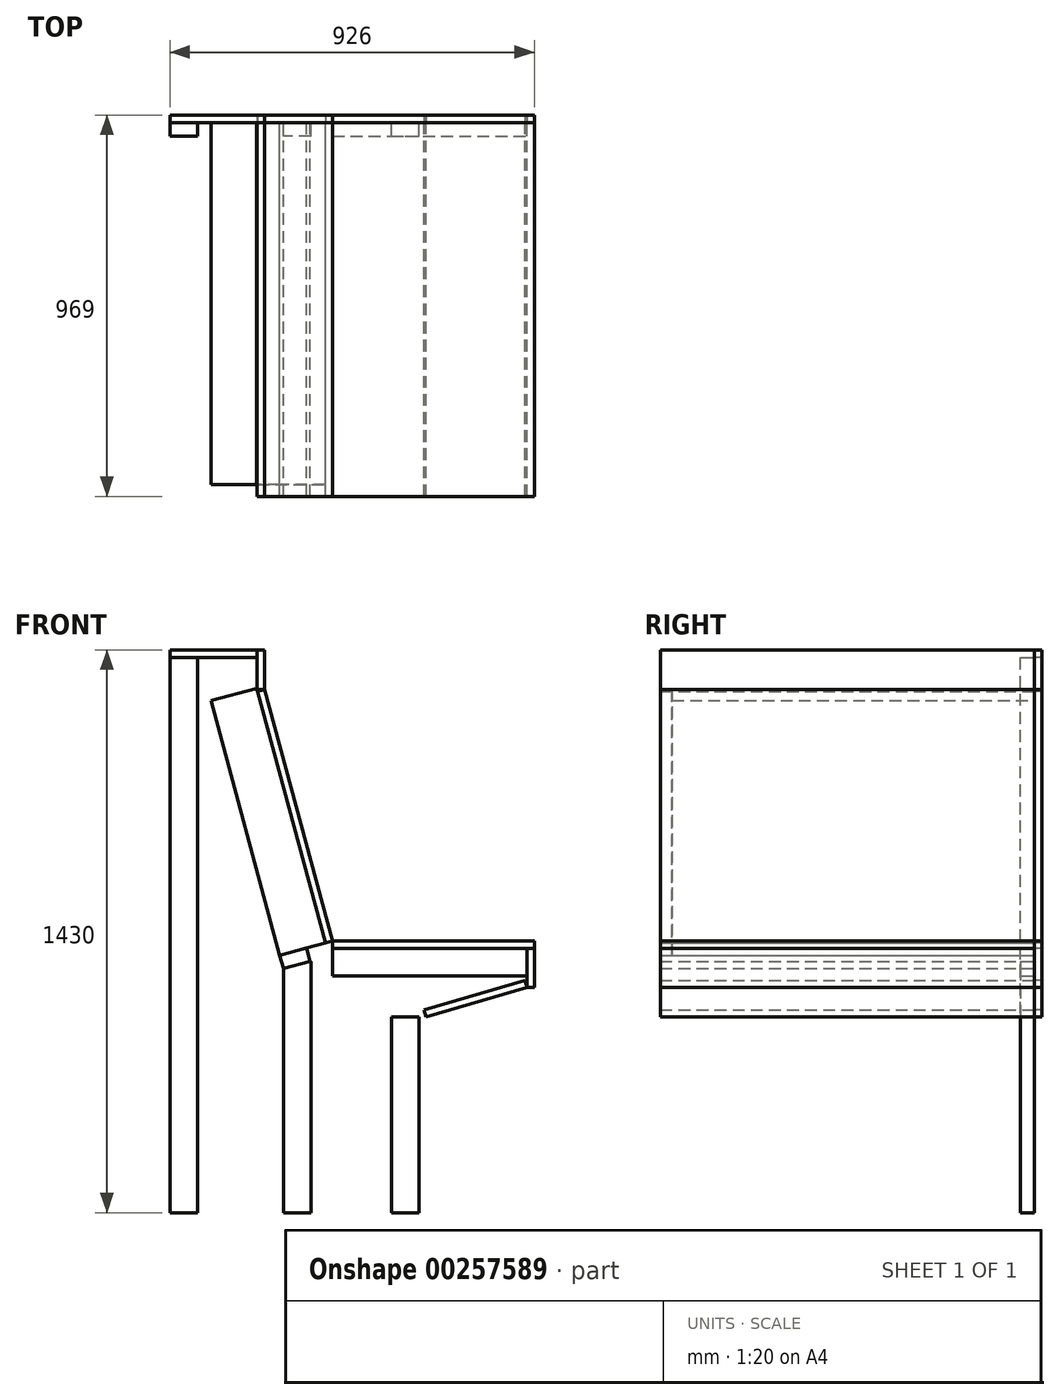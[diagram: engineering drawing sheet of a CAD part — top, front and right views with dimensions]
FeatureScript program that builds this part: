
annotation { "Feature Type Name" : "Feature", "Feature Type Description" : "" }
export const myFeature = defineFeature(function(context is Context, id is Id, definition is map)
    precondition{}
    {
        {
            var Q0;
            Q0=qCreatedBy(makeId("Front.planeOp"),FACE);
            var sketch = newSketch(context, id + "F0", { "sketchPlane" : qUnion([Q0])});
            skLineSegment(sketch, "E0", {"start": v(0, 0) * mm, "end": v(0, 1430) * mm});
            skLineSegment(sketch, "E1", {"start": v(0, 1430) * mm, "end": v(270, 1430) * mm});
            skLineSegment(sketch, "E2", {"start": v(270, 1430) * mm, "end": v(270, 1349.88) * mm});
            skLineSegment(sketch, "E3", {"start": v(275.18, 1310.8) * mm, "end": v(436, 714.79) * mm});
            skLineSegment(sketch, "E4", {"start": v(455.32, 700) * mm, "end": v(935, 700) * mm});
            skLineSegment(sketch, "E5", {"start": v(955, 680) * mm, "end": v(955, 585.01) * mm});
            skLineSegment(sketch, "E6", {"start": v(940.59, 565.8) * mm, "end": v(694.41, 494.2) * mm});
            skLineSegment(sketch, "E7", {"start": v(680, 474.99) * mm, "end": v(680, 0) * mm});
            skLineSegment(sketch, "E8", {"start": v(680, 0) * mm, "end": v(0, 0) * mm});
            skPoint(sketch, "E9.visualSharp", {"position": v(270, 1430) * mm});
            skPoint(sketch, "E10.visualSharp", {"position": v(270, 1330) * mm});
            skArc(sketch, "E10.filletArc", {"start": v(270, 1349.88) * mm, "mid": v(271.3, 1330.17) * mm, "end": v(275.18, 1310.8) * mm});
            skPoint(sketch, "E11.visualSharp", {"position": v(440, 700) * mm});
            skArc(sketch, "E11.filletArc", {"start": v(436, 714.79) * mm, "mid": v(443.16, 704.12) * mm, "end": v(455.32, 700) * mm});
            skPoint(sketch, "E12.visualSharp", {"position": v(955, 700) * mm});
            skArc(sketch, "E12.filletArc", {"start": v(955, 680) * mm, "mid": v(949.14, 694.14) * mm, "end": v(935, 700) * mm});
            skPoint(sketch, "E13.visualSharp", {"position": v(955, 570) * mm});
            skArc(sketch, "E13.filletArc", {"start": v(940.59, 565.8) * mm, "mid": v(951, 573) * mm, "end": v(955, 585.01) * mm});
            skPoint(sketch, "E14.visualSharp", {"position": v(680, 490) * mm});
            skArc(sketch, "E14.filletArc", {"start": v(694.41, 494.2) * mm, "mid": v(684, 487) * mm, "end": v(680, 474.99) * mm});
            skLineSegment(sketch, "E15.bottom", {"start": v(0, 0) * mm, "end": v(19, 0) * mm});
            skLineSegment(sketch, "E15.top", {"start": v(0, 1430) * mm, "end": v(19, 1430) * mm});
            skLineSegment(sketch, "E15.right", {"start": v(19, 0) * mm, "end": v(19, 1430) * mm});
            skLineSegment(sketch, "E16.bottom", {"start": v(670, 0) * mm, "end": v(652, 0) * mm});
            skLineSegment(sketch, "E16.top", {"start": v(670, 497.5) * mm, "end": v(652, 497.5) * mm});
            skLineSegment(sketch, "E16.left", {"start": v(670, 0) * mm, "end": v(670, 497.5) * mm});
            skLineSegment(sketch, "E16.right", {"start": v(652, 0) * mm, "end": v(652, 497.5) * mm});
            skLineSegment(sketch, "E17", {"start": v(670, 497.5) * mm, "end": v(926, 571.98) * mm});
            skLineSegment(sketch, "E18", {"start": v(926, 571.98) * mm, "end": v(920.7, 590.22) * mm});
            skLineSegment(sketch, "E19", {"start": v(920.7, 590.22) * mm, "end": v(664.7, 515.75) * mm});
            skLineSegment(sketch, "E20", {"start": v(664.7, 515.75) * mm, "end": v(670, 497.5) * mm});
            skLineSegment(sketch, "E21.bottom", {"start": v(926, 571.98) * mm, "end": v(945, 571.98) * mm});
            skLineSegment(sketch, "E21.top", {"start": v(926, 671) * mm, "end": v(945, 671) * mm});
            skLineSegment(sketch, "E21.left", {"start": v(926, 571.98) * mm, "end": v(926, 671) * mm});
            skLineSegment(sketch, "E21.right", {"start": v(945, 571.98) * mm, "end": v(945, 671) * mm});
            skLineSegment(sketch, "E22.bottom", {"start": v(945, 671) * mm, "end": v(432.34, 671) * mm});
            skLineSegment(sketch, "E22.top", {"start": v(945, 690) * mm, "end": v(432.34, 690) * mm});
            skLineSegment(sketch, "E22.left", {"start": v(945, 671) * mm, "end": v(945, 690) * mm});
            skLineSegment(sketch, "E22.right", {"start": v(432.34, 671) * mm, "end": v(432.34, 690) * mm});
            skLineSegment(sketch, "E23", {"start": v(432.34, 690) * mm, "end": v(260, 1328.67) * mm});
            skLineSegment(sketch, "E24", {"start": v(260, 1328.67) * mm, "end": v(241.66, 1323.72) * mm});
            skLineSegment(sketch, "E25", {"start": v(241.66, 1323.72) * mm, "end": v(414, 685.05) * mm});
            skLineSegment(sketch, "E26", {"start": v(414, 685.05) * mm, "end": v(432.34, 690) * mm});
            skLineSegment(sketch, "E27.bottom", {"start": v(260, 1328.67) * mm, "end": v(241, 1328.67) * mm});
            skLineSegment(sketch, "E27.top", {"start": v(260, 1430) * mm, "end": v(241, 1430) * mm});
            skLineSegment(sketch, "E27.left", {"start": v(260, 1328.67) * mm, "end": v(260, 1430) * mm});
            skLineSegment(sketch, "E27.right", {"start": v(241, 1328.67) * mm, "end": v(241, 1430) * mm});
            skLineSegment(sketch, "E28.bottom", {"start": v(241, 1430) * mm, "end": v(19, 1430) * mm});
            skLineSegment(sketch, "E28.top", {"start": v(241, 1411) * mm, "end": v(19, 1411) * mm});
            skLineSegment(sketch, "E28.left", {"start": v(241, 1430) * mm, "end": v(241, 1411) * mm});
            skLineSegment(sketch, "E28.right", {"start": v(19, 1430) * mm, "end": v(19, 1411) * mm});
            skSolve(sketch);
        }
        {
            var Q0;
            Q0=makeQuery(id+"F0.imprint","IMPRINT",FACE,{"disambiguationData":[TD([[makeQuery(id+"F0.imprint","IMPRINT",EDGE,{"derivedFrom":sQuery(id+"F0.wireOp",EDGE,"E23")}),1.0]])]});
            var Q1;
            Q1=makeQuery(id+"F0.imprint","IMPRINT",FACE,{"disambiguationData":[TD([[makeQuery(id+"F0.imprint","IMPRINT",EDGE,{"derivedFrom":sQuery(id+"F0.wireOp",EDGE,"E22.top")}),1.0]])]});
            var Q2;
            Q2=makeQuery(id+"F0.imprint","IMPRINT",FACE,{"disambiguationData":[TD([[makeQuery(id+"F0.imprint","IMPRINT",EDGE,{"derivedFrom":sQuery(id+"F0.wireOp",EDGE,"E17")}),1.0]])]});
            var Q3;
            Q3=makeQuery(id+"F0.imprint","IMPRINT",FACE,{"disambiguationData":[TD([[makeQuery(id+"F0.imprint","IMPRINT",EDGE,{"derivedFrom":sQuery(id+"F0.wireOp",EDGE,"E16.bottom")}),-1.0]])]});
            var Q4;
            Q4=makeQuery(id+"F0.imprint","IMPRINT",FACE,{"disambiguationData":[TD([[makeQuery(id+"F0.imprint","IMPRINT",EDGE,{"derivedFrom":sQuery(id+"F0.wireOp",EDGE,"E15.bottom")}),1.0]])]});
            var Q5;
            Q5=makeQuery(id+"F0.imprint","IMPRINT",FACE,{"disambiguationData":[TD([[makeQuery(id+"F0.imprint","IMPRINT",EDGE,{"derivedFrom":sQuery(id+"F0.wireOp",EDGE,"E28.bottom")}),1.0]])]});
            var Q6;
            Q6=makeQuery(id+"F0.imprint","IMPRINT",FACE,{"disambiguationData":[TD([[makeQuery(id+"F0.imprint","IMPRINT",EDGE,{"derivedFrom":sQuery(id+"F0.wireOp",EDGE,"E27.bottom")}),-1.0]])]});
            var Q7;
            Q7=makeQuery(id+"F0.imprint","IMPRINT",FACE,{"disambiguationData":[TD([[makeQuery(id+"F0.imprint","IMPRINT",EDGE,{"derivedFrom":sQuery(id+"F0.wireOp",EDGE,"E1")}),-1.0]])]});
            var Q8;
            Q8=makeQuery(id+"F0.imprint","IMPRINT",FACE,{"disambiguationData":[TD([[makeQuery(id+"F0.imprint","IMPRINT",EDGE,{"derivedFrom":sQuery(id+"F0.wireOp",EDGE,"E21.bottom")}),1.0]])]});
            var Q9;
            {var subQ3=sQuery(id+"F0.wireOp",EDGE,"E15.right");Q9=makeQuery(id+"F0.imprint","IMPRINT",FACE,{"disambiguationData":[TD([[makeQuery(id+"F0.imprint","IMPRINT",EDGE,{"derivedFrom":subQ3}),-1.0]])]});}
            extrude(context, id + "F1", {"entities" : qUnion([Q0, Q1, Q2, Q3, Q4, Q5, Q6, Q7, Q8, Q9]), "oppositeDirection" : true, "depth" : 19 * mm});
        }
        {
            var Q0;
            Q0=makeQuery(id+"F0.imprint","IMPRINT",FACE,{"disambiguationData":[TD([[makeQuery(id+"F0.imprint","IMPRINT",EDGE,{"derivedFrom":sQuery(id+"F0.wireOp",EDGE,"E15.bottom")}),1.0]])]});
            var Q1;
            Q1=makeQuery(id+"F0.imprint","IMPRINT",FACE,{"disambiguationData":[TD([[makeQuery(id+"F0.imprint","IMPRINT",EDGE,{"derivedFrom":sQuery(id+"F0.wireOp",EDGE,"E16.bottom")}),-1.0]])]});
            var Q2;
            Q2=makeQuery(id+"F0.imprint","IMPRINT",FACE,{"disambiguationData":[TD([[makeQuery(id+"F0.imprint","IMPRINT",EDGE,{"derivedFrom":sQuery(id+"F0.wireOp",EDGE,"E17")}),1.0]])]});
            var Q3;
            Q3=makeQuery(id+"F0.imprint","IMPRINT",FACE,{"disambiguationData":[TD([[makeQuery(id+"F0.imprint","IMPRINT",EDGE,{"derivedFrom":sQuery(id+"F0.wireOp",EDGE,"E22.top")}),1.0]])]});
            var Q4;
            Q4=makeQuery(id+"F0.imprint","IMPRINT",FACE,{"disambiguationData":[TD([[makeQuery(id+"F0.imprint","IMPRINT",EDGE,{"derivedFrom":sQuery(id+"F0.wireOp",EDGE,"E23")}),1.0]])]});
            var Q5;
            Q5=makeQuery(id+"F0.imprint","IMPRINT",FACE,{"disambiguationData":[TD([[makeQuery(id+"F0.imprint","IMPRINT",EDGE,{"derivedFrom":sQuery(id+"F0.wireOp",EDGE,"E27.bottom")}),-1.0]])]});
            extrude(context, id + "F2", {"entities" : qUnion([Q0, Q1, Q2, Q3, Q4, Q5]), "depth" : 950 * mm});
        }
        {
            var Q0;
            Q0=makeQuery(id+"F0.imprint","IMPRINT",FACE,{"disambiguationData":[TD([[makeQuery(id+"F0.imprint","IMPRINT",EDGE,{"derivedFrom":sQuery(id+"F0.wireOp",EDGE,"E21.bottom")}),1.0]])]});
            var Q1;
            Q1=makeQuery(id+"F0.imprint","IMPRINT",FACE,{"disambiguationData":[TD([[makeQuery(id+"F0.imprint","IMPRINT",EDGE,{"derivedFrom":sQuery(id+"F0.wireOp",EDGE,"E28.bottom")}),1.0]])]});
            extrude(context, id + "F3", {"entities" : qUnion([Q0, Q1]), "depth" : 950 * mm});
        }
        {
            var Q0;
            Q0=qCreatedBy(makeId("Front.planeOp"),FACE);
            var sketch = newSketch(context, id + "F4", { "sketchPlane" : qUnion([Q0])});
            skLineSegment(sketch, "E29", {"start": v(239.45, 1331.91) * mm, "end": v(414, 685.05) * mm});
            skLineSegment(sketch, "E30", {"start": v(414, 685.05) * mm, "end": v(298.14, 653.79) * mm});
            skLineSegment(sketch, "E31", {"start": v(298.14, 653.79) * mm, "end": v(123.6, 1300.65) * mm});
            skLineSegment(sketch, "E32", {"start": v(123.6, 1300.65) * mm, "end": v(239.45, 1331.91) * mm});
            skSolve(sketch);
        }
        {
            var Q0;
            Q0 = qSketchRegion(id + "F4", true);
            extrude(context, id + "F5", {"entities" : qUnion([Q0]), "depth" : 920 * mm});
        }
        {
            var Q0;
            Q0=qCreatedBy(makeId("Front.planeOp"),FACE);
            var sketch = newSketch(context, id + "F6", { "sketchPlane" : qUnion([Q0])});
            skLineSegment(sketch, "E33.bottom", {"start": v(89, 0) * mm, "end": v(19, 0) * mm});
            skLineSegment(sketch, "E33.top", {"start": v(89, 1411) * mm, "end": v(19, 1411) * mm});
            skLineSegment(sketch, "E33.left", {"start": v(89, 0) * mm, "end": v(89, 1411) * mm});
            skLineSegment(sketch, "E33.right", {"start": v(19, 0) * mm, "end": v(19, 1411) * mm});
            skLineSegment(sketch, "E34.bottom", {"start": v(582, 0) * mm, "end": v(652, 0) * mm});
            skLineSegment(sketch, "E34.top", {"start": v(582, 497.5) * mm, "end": v(652, 497.5) * mm});
            skLineSegment(sketch, "E34.left", {"start": v(582, 0) * mm, "end": v(582, 497.5) * mm});
            skLineSegment(sketch, "E34.right", {"start": v(652, 0) * mm, "end": v(652, 497.5) * mm});
            skLineSegment(sketch, "E35.bottom", {"start": v(432.34, 601) * mm, "end": v(926, 601) * mm});
            skLineSegment(sketch, "E35.top", {"start": v(432.34, 671) * mm, "end": v(926, 671) * mm});
            skLineSegment(sketch, "E35.left", {"start": v(432.34, 601) * mm, "end": v(432.34, 671) * mm});
            skLineSegment(sketch, "E35.right", {"start": v(926, 601) * mm, "end": v(926, 671) * mm});
            skLineSegment(sketch, "E36", {"start": v(298.14, 653.79) * mm, "end": v(307.26, 620) * mm});
            skLineSegment(sketch, "E37", {"start": v(307.26, 620) * mm, "end": v(374.84, 638.23) * mm});
            skLineSegment(sketch, "E38", {"start": v(374.84, 638.23) * mm, "end": v(365.72, 672.02) * mm});
            skLineSegment(sketch, "E39", {"start": v(365.72, 672.02) * mm, "end": v(298.14, 653.79) * mm});
            skLineSegment(sketch, "E40", {"start": v(307.26, 620) * mm, "end": v(307.26, 0) * mm});
            skLineSegment(sketch, "E41", {"start": v(377.26, 0) * mm, "end": v(377.26, 638.88) * mm});
            skLineSegment(sketch, "E42", {"start": v(377.26, 638.88) * mm, "end": v(307.26, 620) * mm});
            skLineSegment(sketch, "E43", {"start": v(307.26, 0) * mm, "end": v(377.26, 0) * mm});
            skSolve(sketch);
        }
        {
            var Q0;
            Q0=makeQuery(id+"F6.imprint","IMPRINT",FACE,{"disambiguationData":[TD([[makeQuery(id+"F6.imprint","IMPRINT",EDGE,{"derivedFrom":sQuery(id+"F6.wireOp",EDGE,"E33.bottom")}),-1.0]])]});
            var Q1;
            {var subQ3=sQuery(id+"F6.wireOp",EDGE,"E40");Q1=makeQuery(id+"F6.imprint","IMPRINT",FACE,{"disambiguationData":[TD([[makeQuery(id+"F6.imprint","IMPRINT",EDGE,{"derivedFrom":subQ3}),1.0]])]});}
            var Q2;
            Q2=makeQuery(id+"F6.imprint","IMPRINT",FACE,{"disambiguationData":[TD([[makeQuery(id+"F6.imprint","IMPRINT",EDGE,{"derivedFrom":sQuery(id+"F6.wireOp",EDGE,"E34.bottom")}),1.0]])]});
            var Q3;
            Q3=makeQuery(id+"F6.imprint","IMPRINT",FACE,{"disambiguationData":[TD([[makeQuery(id+"F6.imprint","IMPRINT",EDGE,{"derivedFrom":sQuery(id+"F6.wireOp",EDGE,"E35.bottom")}),1.0]])]});
            extrude(context, id + "F7", {"entities" : qUnion([Q0, Q1, Q2, Q3]), "depth" : 35 * mm});
        }
        {
            var Q0;
            {var subQ0=sQuery(id+"F6.wireOp",EDGE,"E36");Q0=makeQuery(id+"F6.imprint","IMPRINT",FACE,{"disambiguationData":[TD([[makeQuery(id+"F6.imprint","IMPRINT",EDGE,{"derivedFrom":subQ0}),1.0]])]});}
            extrude(context, id + "F8", {"entities" : qUnion([Q0]), "depth" : 950 * mm});
        }
    });
